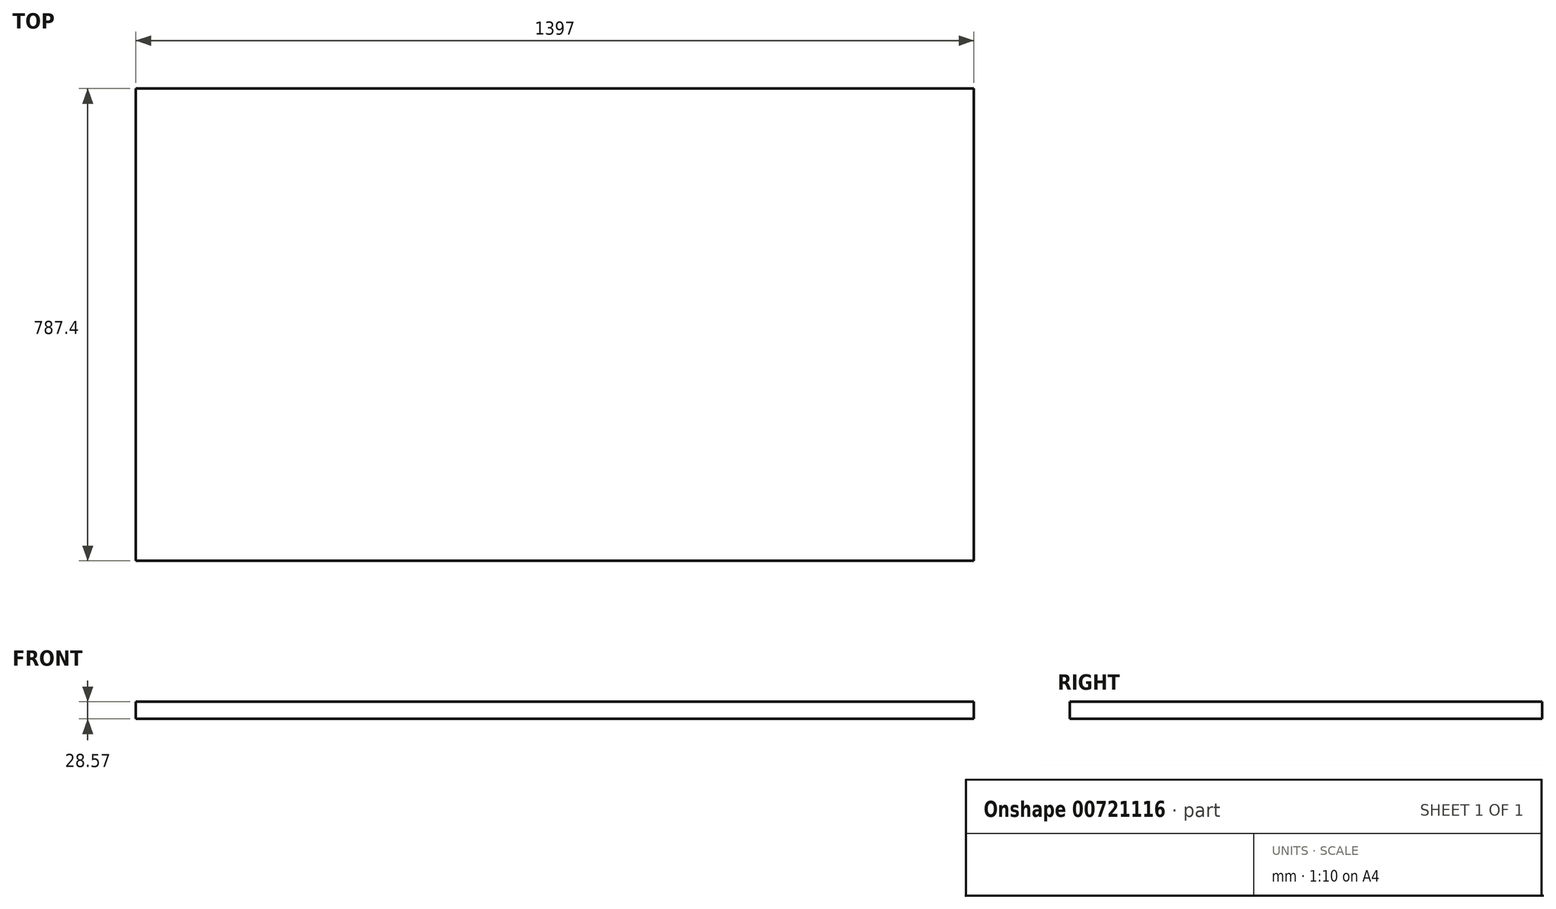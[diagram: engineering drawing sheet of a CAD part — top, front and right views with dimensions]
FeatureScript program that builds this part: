
annotation { "Feature Type Name" : "Feature", "Feature Type Description" : "" }
export const myFeature = defineFeature(function(context is Context, id is Id, definition is map)
    precondition{}
    {
        {
            var Q0;
            Q0=qCreatedBy(makeId("Top.planeOp"),FACE);
            var sketch = newSketch(context, id + "F0", { "sketchPlane" : qUnion([Q0])});
            skLineSegment(sketch, "E0.bottom", {"start": v(-698.5, 393.7) * mm, "end": v(698.5, 393.7) * mm});
            skLineSegment(sketch, "E0.top", {"start": v(-698.5, -393.7) * mm, "end": v(698.5, -393.7) * mm});
            skLineSegment(sketch, "E0.left", {"start": v(-698.5, 393.7) * mm, "end": v(-698.5, -393.7) * mm});
            skLineSegment(sketch, "E0.right", {"start": v(698.5, 393.7) * mm, "end": v(698.5, -393.7) * mm});
            skPoint(sketch, "E0.middle", {"position": v(0, 0) * mm});
            skSolve(sketch);
        }
        {
            var Q0;
            Q0=makeQuery(id+"F0.imprint","IMPRINT",FACE,{"disambiguationData":[TD([[makeQuery(id+"F0.imprint","IMPRINT",EDGE,{"derivedFrom":sQuery(id+"F0.wireOp",EDGE,"E0.bottom")}),-1.0]])]});
            extrude(context, id + "F1", {"entities" : qUnion([Q0]), "depth" : 28.57 * mm, "offsetDistance" : 25.4 * mm});
        }
    });
